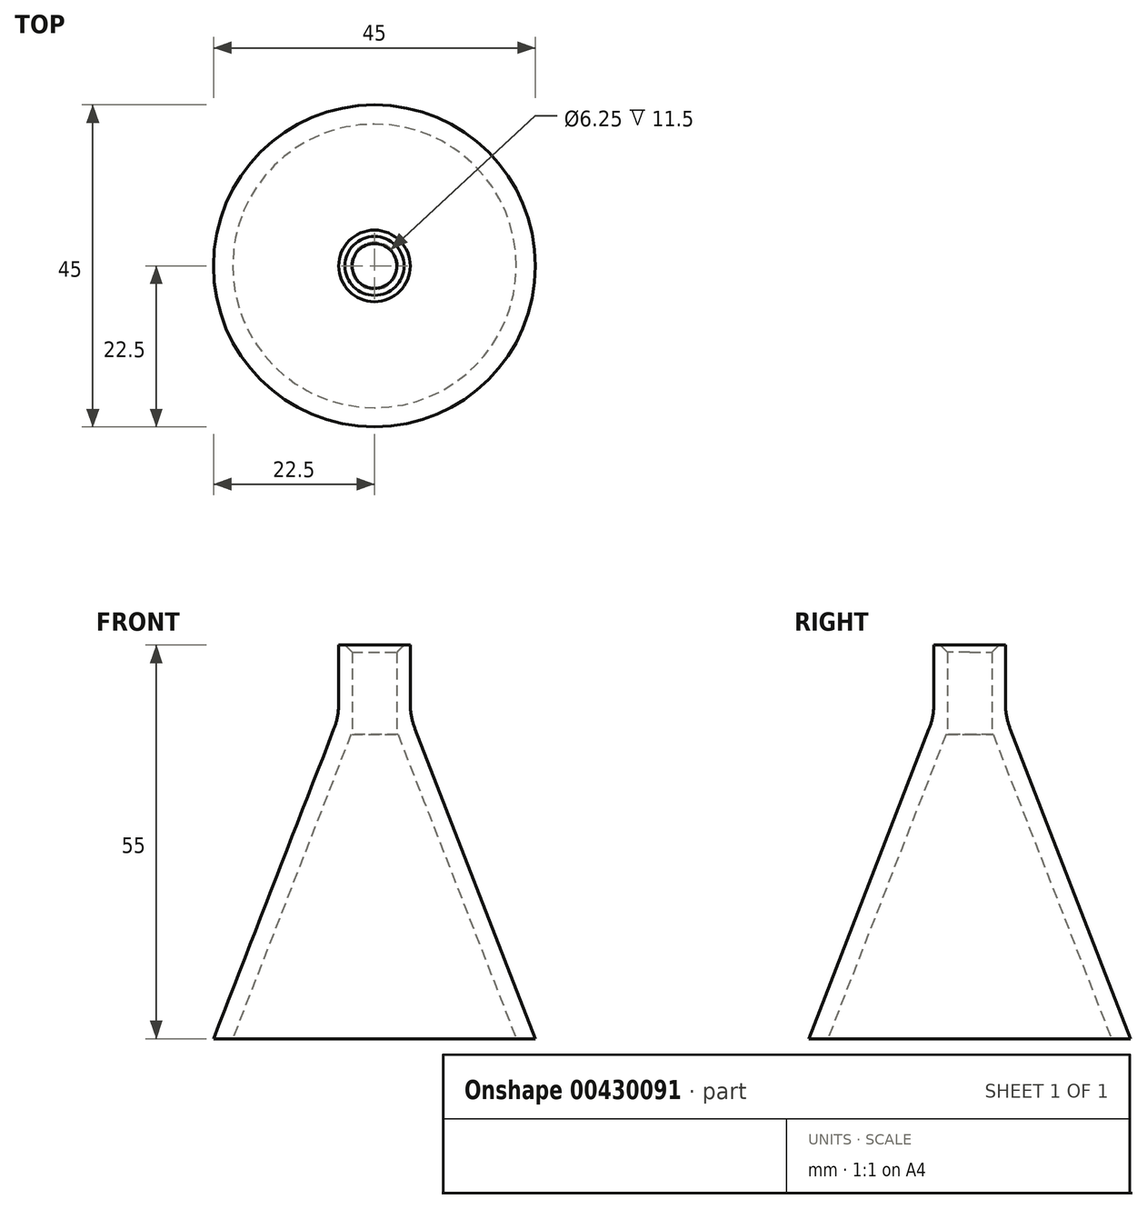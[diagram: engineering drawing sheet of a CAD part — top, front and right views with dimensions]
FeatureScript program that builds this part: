
annotation { "Feature Type Name" : "Feature", "Feature Type Description" : "" }
export const myFeature = defineFeature(function(context is Context, id is Id, definition is map)
    precondition{}
    {
        {
            var Q0;
            Q0=qCreatedBy(makeId("Top.planeOp"),FACE);
            var sketch = newSketch(context, id + "F0", { "sketchPlane" : qUnion([Q0])});
            skCircle(sketch, "E0", {"center": v(0, 0) * mm, "radius": 22.5 * mm});
            skSolve(sketch);
        }
        {
            var Q0;
            Q0=qCreatedBy(makeId("Top.planeOp"),FACE);
            cPlane(context, id + "F1", {"entities" : qUnion([Q0]), "cplaneType" : CPlaneType.OFFSET, "offset" : 45 * mm, "width" : 150 * mm, "height" : 150 * mm});
        }
        {
            var Q0;
            Q0=qCreatedBy(id+"F1.planeOp",FACE);
            var sketch = newSketch(context, id + "F2", { "sketchPlane" : qUnion([Q0])});
            skCircle(sketch, "E1", {"center": v(0, 0) * mm, "radius": 5 * mm});
            skSolve(sketch);
        }
        {
            var Q0;
            Q0=makeQuery(id+"F2.imprint","IMPRINT",FACE,{"disambiguationData":[TD([[makeQuery(id+"F2.imprint","IMPRINT",EDGE,{"derivedFrom":sQuery(id+"F2.wireOp",EDGE,"E1")}),1.0]])]});
            var Q1;
            Q1=makeQuery(id+"F0.imprint","IMPRINT",FACE,{"disambiguationData":[TD([[makeQuery(id+"F0.imprint","IMPRINT",EDGE,{"derivedFrom":sQuery(id+"F0.wireOp",EDGE,"E0")}),1.0]])]});
            loft(context, id + "F3", {"sheetProfilesArray" : [{ "sheetProfileEntities" : qUnion([Q0]) }, { "sheetProfileEntities" : qUnion([Q1]) }]});
        }
        {
            var Q0;
            Q0=makeQuery(id+"F3.opLoft","CAP_FACE",FACE,{"disambiguationData":[OSD([makeQuery(id+"F0.imprint","IMPRINT",FACE,{"disambiguationData":[TD([[makeQuery(id+"F0.imprint","IMPRINT",EDGE,{"derivedFrom":sQuery(id+"F0.wireOp",EDGE,"E0")}),1.0]])]})])],"isStart":true});
            shell(context, id + "F4", {"entities" : qUnion([Q0]), "thickness" : 2.5 * mm});
        }
        {
            var Q0;
            Q0=makeQuery(id+"F3.opLoft","CAP_FACE",FACE,{"disambiguationData":[OSD([makeQuery(id+"F2.imprint","IMPRINT",FACE,{"disambiguationData":[TD([[makeQuery(id+"F2.imprint","IMPRINT",EDGE,{"derivedFrom":sQuery(id+"F2.wireOp",EDGE,"E1")}),1.0]])]})])],"isStart":true});
            var sketch = newSketch(context, id + "F5", { "sketchPlane" : qUnion([Q0])});
            skCircle(sketch, "E2", {"center": v(0, 0) * mm, "radius": 3.12 * mm});
            skSolve(sketch);
        }
        {
            var Q0;
            Q0=makeQuery(id+"F5.imprint","IMPRINT",FACE,{"disambiguationData":[TD([[makeQuery(id+"F5.imprint","IMPRINT",EDGE,{"derivedFrom":sQuery(id+"F5.wireOp",EDGE,"E2")}),-1.0]])]});
            extrude(context, id + "F6", {"entities" : qUnion([Q0]), "operationType" : NewBodyOperationType.ADD, "depth" : 10 * mm});
        }
        {
            var Q0;
            Q0=makeQuery(id+"F4.opShell","OFFSET_FACE",FACE,{"disambiguationData":[OSD([makeQuery(id+"F2.imprint","IMPRINT",FACE,{"disambiguationData":[TD([[makeQuery(id+"F2.imprint","IMPRINT",EDGE,{"derivedFrom":sQuery(id+"F2.wireOp",EDGE,"E1")}),1.0]])]})])]});
            var sketch = newSketch(context, id + "F7", { "sketchPlane" : qUnion([Q0])});
            skPoint(sketch, "E3", {"position": v(0, 0) * mm});
            skSolve(sketch);
        }
        {
            var Q0;
            Q0=sQuery(id+"F7.wireOp",VERTEX,"E3");
            var Q1;
            Q1=makeQuery(id+"F3.opLoft","SWEPT_BODY",BODY,{"disambiguationData":[OSD([makeQuery(id+"F0.imprint","IMPRINT",FACE,{"disambiguationData":[TD([[makeQuery(id+"F0.imprint","IMPRINT",EDGE,{"derivedFrom":sQuery(id+"F0.wireOp",EDGE,"E0")}),1.0]])]}),makeQuery(id+"F2.imprint","IMPRINT",FACE,{"disambiguationData":[TD([[makeQuery(id+"F2.imprint","IMPRINT",EDGE,{"derivedFrom":sQuery(id+"F2.wireOp",EDGE,"E1")}),1.0]])]})])]});
            hole(context, id + "F8", {"style" : HoleStyle.SIMPLE, "endStyle" : HoleEndStyle.BLIND, "holeDiameter" : 6.25 * mm, "holeDepth" : 10 * mm, "isTappedThrough" : true, "tappedDepth" : 12 * mm, "tapClearance" : 3, "locations" : qUnion([Q0]), "scope" : qUnion([Q1])});
        }
        {
            var Q0;
            Q0=makeQuery(id+"F6.opExtrude","CAP_EDGE",EDGE,{"disambiguationData":[OSD([sQuery(id+"F5.wireOp",EDGE,"E2")])],"isStart":false});
            chamfer(context, id + "F9", {"entities" : qUnion([Q0]), "width" : 1 * mm, "tangentPropagation" : true});
        }
        {
            var Q0;
            {var subQ0=sQuery(id+"F2.wireOp",EDGE,"E1");Q0=makeQuery(id+"F6.boolean.opBoolean","MERGE",EDGE,{"derivedFrom":[makeQuery(id+"F3.opLoft","MID_CAP_EDGE",EDGE,{"disambiguationData":[OSD([subQ0])],"capPos":0.0}),makeQuery(id+"F6.opExtrude","CAP_EDGE",EDGE,{"disambiguationData":[OSD([subQ0])],"isStart":true})]});}
            fillet(context, id + "F10", {"entities" : qUnion([Q0]), "radius" : 10 * mm, "tangentPropagation" : true, "allowEdgeOverflow" : false});
        }
    });
